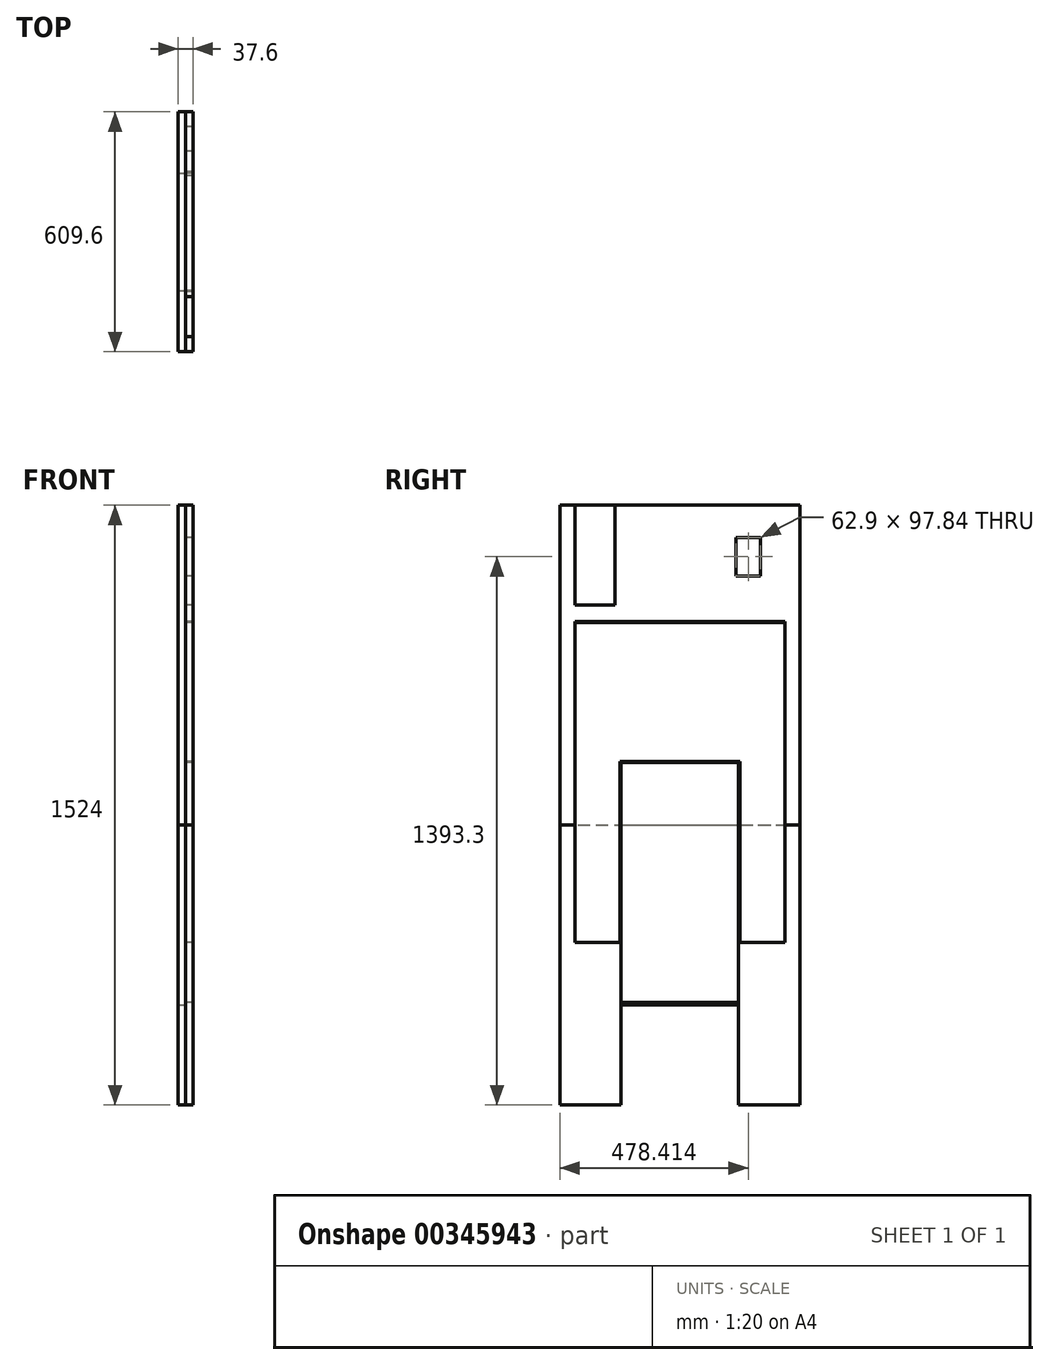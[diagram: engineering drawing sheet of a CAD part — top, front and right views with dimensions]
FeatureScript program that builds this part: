
annotation { "Feature Type Name" : "Feature", "Feature Type Description" : "" }
export const myFeature = defineFeature(function(context is Context, id is Id, definition is map)
    precondition{}
    {
        {
            var Q0;
            Q0=qCreatedBy(makeId("Right.planeOp"),FACE);
            var sketch = newSketch(context, id + "F0", { "sketchPlane" : qUnion([Q0])});
            skLineSegment(sketch, "E0.bottom", {"start": v(0, 0) * mm, "end": v(609.6, 0) * mm});
            skLineSegment(sketch, "E0.top", {"start": v(0, 1524) * mm, "end": v(609.6, 1524) * mm});
            skLineSegment(sketch, "E0.left", {"start": v(0, 0) * mm, "end": v(0, 1524) * mm});
            skLineSegment(sketch, "E0.right", {"start": v(609.6, 0) * mm, "end": v(609.6, 1524) * mm});
            skLineSegment(sketch, "E1", {"start": v(139.7, 1524) * mm, "end": v(139.7, 1270) * mm});
            skLineSegment(sketch, "E2", {"start": v(139.7, 1270) * mm, "end": v(0, 1270) * mm});
            skLineSegment(sketch, "E3.bottom", {"start": v(509.86, 1442.22) * mm, "end": v(446.97, 1442.22) * mm});
            skLineSegment(sketch, "E3.top", {"start": v(509.86, 1344.38) * mm, "end": v(446.97, 1344.38) * mm});
            skLineSegment(sketch, "E3.left", {"start": v(509.86, 1442.22) * mm, "end": v(509.86, 1344.38) * mm});
            skLineSegment(sketch, "E3.right", {"start": v(446.97, 1442.22) * mm, "end": v(446.97, 1344.38) * mm});
            skLineSegment(sketch, "E4", {"start": v(38.1, 1225.55) * mm, "end": v(38.1, 412.75) * mm});
            skLineSegment(sketch, "E5", {"start": v(38.1, 412.75) * mm, "end": v(152.4, 412.75) * mm});
            skLineSegment(sketch, "E6", {"start": v(152.4, 412.75) * mm, "end": v(152.4, 873.12) * mm});
            skLineSegment(sketch, "E7", {"start": v(152.4, 873.12) * mm, "end": v(457.2, 873.12) * mm});
            skLineSegment(sketch, "E8", {"start": v(457.2, 873.12) * mm, "end": v(457.2, 412.75) * mm});
            skLineSegment(sketch, "E9", {"start": v(457.2, 412.75) * mm, "end": v(571.5, 412.75) * mm});
            skLineSegment(sketch, "E10", {"start": v(571.5, 412.75) * mm, "end": v(571.5, 1225.55) * mm});
            skLineSegment(sketch, "E11", {"start": v(571.5, 1225.55) * mm, "end": v(463.88, 1225.55) * mm});
            skLineSegment(sketch, "E12", {"start": v(463.88, 1225.55) * mm, "end": v(463.88, 1169.64) * mm});
            skLineSegment(sketch, "E13", {"start": v(463.88, 1169.64) * mm, "end": v(403.31, 1169.64) * mm});
            skLineSegment(sketch, "E14", {"start": v(403.31, 1169.64) * mm, "end": v(403.31, 1225.55) * mm});
            skLineSegment(sketch, "E15", {"start": v(403.31, 1225.55) * mm, "end": v(206.29, 1225.55) * mm});
            skLineSegment(sketch, "E16", {"start": v(206.29, 1225.55) * mm, "end": v(206.29, 1169.64) * mm});
            skLineSegment(sketch, "E17", {"start": v(206.29, 1169.64) * mm, "end": v(145.72, 1169.64) * mm});
            skLineSegment(sketch, "E18", {"start": v(145.72, 1169.64) * mm, "end": v(145.72, 1225.55) * mm});
            skLineSegment(sketch, "E19", {"start": v(145.72, 1225.55) * mm, "end": v(38.1, 1225.55) * mm});
            skLineSegment(sketch, "E20.bottom", {"start": v(155.58, 869.95) * mm, "end": v(454.02, 869.95) * mm});
            skLineSegment(sketch, "E20.top", {"start": v(155.58, 260.35) * mm, "end": v(454.02, 260.35) * mm});
            skLineSegment(sketch, "E20.left", {"start": v(155.58, 869.95) * mm, "end": v(155.58, 260.35) * mm});
            skLineSegment(sketch, "E20.right", {"start": v(454.02, 869.95) * mm, "end": v(454.02, 260.35) * mm});
            skLineSegment(sketch, "E21.bottom", {"start": v(155.58, 0) * mm, "end": v(454.02, 0) * mm});
            skLineSegment(sketch, "E21.top", {"start": v(155.58, 254) * mm, "end": v(454.02, 254) * mm});
            skLineSegment(sketch, "E21.left", {"start": v(155.58, 0) * mm, "end": v(155.58, 254) * mm});
            skLineSegment(sketch, "E21.right", {"start": v(454.02, 0) * mm, "end": v(454.02, 254) * mm});
            skLineSegment(sketch, "E22", {"start": v(38.1, 1225.55) * mm, "end": v(0, 1225.55) * mm, "construction": true});
            skLineSegment(sketch, "E23", {"start": v(609.6, 1225.55) * mm, "end": v(571.5, 1225.55) * mm, "construction": true});
            skLineSegment(sketch, "E24", {"start": v(155.58, 873.12) * mm, "end": v(155.58, 869.95) * mm, "construction": true});
            skLineSegment(sketch, "E25", {"start": v(155.58, 869.95) * mm, "end": v(152.4, 869.95) * mm, "construction": true});
            skLineSegment(sketch, "E26", {"start": v(454.02, 869.95) * mm, "end": v(457.2, 869.95) * mm, "construction": true});
            skLineSegment(sketch, "E27", {"start": v(145.72, 1225.55) * mm, "end": v(463.88, 1225.55) * mm});
            skLineSegment(sketch, "E28", {"start": v(38.1, 1524) * mm, "end": v(38.1, 1270) * mm});
            skLineSegment(sketch, "E29", {"start": v(0, 711.2) * mm, "end": v(38.1, 711.2) * mm});
            skLineSegment(sketch, "E30", {"start": v(571.5, 711.2) * mm, "end": v(609.6, 711.2) * mm});
            skLineSegment(sketch, "E31", {"start": v(38.1, 711.2) * mm, "end": v(571.5, 711.2) * mm});
            skLineSegment(sketch, "E32", {"start": v(571.5, 1225.55) * mm, "end": v(571.5, 1228.73) * mm});
            skLineSegment(sketch, "E33", {"start": v(571.5, 1228.73) * mm, "end": v(38.1, 1228.73) * mm});
            skLineSegment(sketch, "E34", {"start": v(38.1, 1228.73) * mm, "end": v(38.1, 1225.55) * mm});
            skLineSegment(sketch, "E35", {"start": v(155.57, 260.35) * mm, "end": v(155.57, 254) * mm});
            skLineSegment(sketch, "E36", {"start": v(454.02, 260.35) * mm, "end": v(454.02, 254) * mm});
            skLineSegment(sketch, "E37", {"start": v(152.4, 412.75) * mm, "end": v(155.58, 412.75) * mm});
            skLineSegment(sketch, "E38", {"start": v(454.02, 412.75) * mm, "end": v(457.2, 412.75) * mm});
            skSolve(sketch);
        }
        {
            var Q0;
            {var subQ12=sQuery(id+"F0.wireOp",EDGE,"E5");Q0=makeQuery(id+"F0.imprint","IMPRINT",FACE,{"disambiguationData":[TD([[makeQuery(id+"F0.imprint","IMPRINT",EDGE,{"derivedFrom":subQ12}),-1.0]])]});}
            var Q1;
            Q1=makeQuery(id+"F0.imprint","IMPRINT",FACE,{"disambiguationData":[TD([[makeQuery(id+"F0.imprint","IMPRINT",EDGE,{"derivedFrom":sQuery(id+"F0.wireOp",EDGE,"E21.bottom")}),1.0]])]});
            var Q2;
            {var subQ0=sQuery(id+"F0.wireOp",EDGE,"E20.top");Q2=makeQuery(id+"F0.imprint","IMPRINT",FACE,{"disambiguationData":[TD([[makeQuery(id+"F0.imprint","IMPRINT",EDGE,{"derivedFrom":subQ0}),1.0]])]});}
            var Q3;
            {var subQ0=sQuery(id+"F0.wireOp",EDGE,"E5");Q3=makeQuery(id+"F0.imprint","IMPRINT",FACE,{"disambiguationData":[TD([[makeQuery(id+"F0.imprint","IMPRINT",EDGE,{"derivedFrom":subQ0}),1.0]])]});}
            var Q4;
            Q4=makeQuery(id+"F0.imprint","IMPRINT",FACE,{"disambiguationData":[TD([[makeQuery(id+"F0.imprint","IMPRINT",EDGE,{"derivedFrom":sQuery(id+"F0.wireOp",EDGE,"E20.top")}),-1.0]])]});
            var Q5;
            {var subQ0=sQuery(id+"F0.wireOp",EDGE,"E9");Q5=makeQuery(id+"F0.imprint","IMPRINT",FACE,{"disambiguationData":[TD([[makeQuery(id+"F0.imprint","IMPRINT",EDGE,{"derivedFrom":subQ0}),-1.0]])]});}
            var Q6;
            {var subQ0=sQuery(id+"F0.wireOp",EDGE,"E9");Q6=makeQuery(id+"F0.imprint","IMPRINT",FACE,{"disambiguationData":[TD([[makeQuery(id+"F0.imprint","IMPRINT",EDGE,{"derivedFrom":subQ0}),1.0]])]});}
            var Q7;
            {var subQ0=sQuery(id+"F0.wireOp",EDGE,"E38");Q7=makeQuery(id+"F0.imprint","IMPRINT",FACE,{"disambiguationData":[TD([[makeQuery(id+"F0.imprint","IMPRINT",EDGE,{"derivedFrom":subQ0}),1.0]])]});}
            var Q8;
            {var subQ0=sQuery(id+"F0.wireOp",EDGE,"E37");Q8=makeQuery(id+"F0.imprint","IMPRINT",FACE,{"disambiguationData":[TD([[makeQuery(id+"F0.imprint","IMPRINT",EDGE,{"derivedFrom":subQ0}),1.0]])]});}
            extrude(context, id + "F1", {"entities" : qUnion([Q0, Q1, Q2, Q3, Q4, Q5, Q6, Q7, Q8]), "oppositeDirection" : true, "depth" : 18.8 * mm});
        }
        {
            var Q0;
            Q0=makeQuery(id+"F0.imprint","IMPRINT",FACE,{"disambiguationData":[TD([[makeQuery(id+"F0.imprint","IMPRINT",EDGE,{"derivedFrom":sQuery(id+"F0.wireOp",EDGE,"E21.bottom")}),1.0]])]});
            var Q1;
            {var subQ0=sQuery(id+"F0.wireOp",EDGE,"E20.top");Q1=makeQuery(id+"F0.imprint","IMPRINT",FACE,{"disambiguationData":[TD([[makeQuery(id+"F0.imprint","IMPRINT",EDGE,{"derivedFrom":subQ0}),1.0]])]});}
            var Q2;
            {var subQ10=sQuery(id+"F0.wireOp",EDGE,"E7");Q2=makeQuery(id+"F0.imprint","IMPRINT",FACE,{"disambiguationData":[TD([[makeQuery(id+"F0.imprint","IMPRINT",EDGE,{"derivedFrom":subQ10}),1.0]])]});}
            var Q3;
            {var subQ0=sQuery(id+"F0.wireOp",EDGE,"E9");Q3=makeQuery(id+"F0.imprint","IMPRINT",FACE,{"disambiguationData":[TD([[makeQuery(id+"F0.imprint","IMPRINT",EDGE,{"derivedFrom":subQ0}),1.0]])]});}
            var Q4;
            {var subQ0=sQuery(id+"F0.wireOp",EDGE,"E5");Q4=makeQuery(id+"F0.imprint","IMPRINT",FACE,{"disambiguationData":[TD([[makeQuery(id+"F0.imprint","IMPRINT",EDGE,{"derivedFrom":subQ0}),1.0]])]});}
            var Q5;
            {var subQ0=sQuery(id+"F0.wireOp",EDGE,"E16");Q5=makeQuery(id+"F0.imprint","IMPRINT",FACE,{"disambiguationData":[TD([[makeQuery(id+"F0.imprint","IMPRINT",EDGE,{"derivedFrom":subQ0}),-1.0]])]});}
            var Q6;
            {var subQ0=sQuery(id+"F0.wireOp",EDGE,"E12");Q6=makeQuery(id+"F0.imprint","IMPRINT",FACE,{"disambiguationData":[TD([[makeQuery(id+"F0.imprint","IMPRINT",EDGE,{"derivedFrom":subQ0}),-1.0]])]});}
            var Q7;
            {var subQ0=sQuery(id+"F0.wireOp",EDGE,"E20.bottom");Q7=makeQuery(id+"F0.imprint","IMPRINT",FACE,{"disambiguationData":[TD([[makeQuery(id+"F0.imprint","IMPRINT",EDGE,{"derivedFrom":subQ0}),-1.0]])]});}
            extrude(context, id + "F2", {"entities" : qUnion([Q0, Q1, Q2, Q3, Q4, Q5, Q6, Q7]), "depth" : 18.8 * mm});
        }
        {
            var Q0;
            {var subQ0=sQuery(id+"F0.wireOp",EDGE,"E9");Q0=makeQuery(id+"F0.imprint","IMPRINT",FACE,{"disambiguationData":[TD([[makeQuery(id+"F0.imprint","IMPRINT",EDGE,{"derivedFrom":subQ0}),-1.0]])]});}
            var Q1;
            {var subQ0=sQuery(id+"F0.wireOp",EDGE,"E5");Q1=makeQuery(id+"F0.imprint","IMPRINT",FACE,{"disambiguationData":[TD([[makeQuery(id+"F0.imprint","IMPRINT",EDGE,{"derivedFrom":subQ0}),-1.0]])]});}
            extrude(context, id + "F3", {"entities" : qUnion([Q0, Q1]), "depth" : 18.8 * mm});
        }
        {
            var Q0;
            {var subQ5=sQuery(id+"F0.wireOp",EDGE,"E1");Q0=makeQuery(id+"F0.imprint","IMPRINT",FACE,{"disambiguationData":[TD([[makeQuery(id+"F0.imprint","IMPRINT",EDGE,{"derivedFrom":subQ5}),1.0]])]});}
            var Q1;
            {var subQ3=sQuery(id+"F0.wireOp",EDGE,"E28");Q1=makeQuery(id+"F0.imprint","IMPRINT",FACE,{"disambiguationData":[TD([[makeQuery(id+"F0.imprint","IMPRINT",EDGE,{"derivedFrom":subQ3}),-1.0]])]});}
            extrude(context, id + "F4", {"entities" : qUnion([Q0, Q1]), "depth" : 18.8 * mm});
        }
        {
            var Q0;
            {var subQ0=sQuery(id+"F0.wireOp",EDGE,"E1");Q0=makeQuery(id+"F0.imprint","IMPRINT",FACE,{"disambiguationData":[TD([[makeQuery(id+"F0.imprint","IMPRINT",EDGE,{"derivedFrom":subQ0}),-1.0]])]});}
            var Q1;
            Q1=makeQuery(id+"F0.imprint","IMPRINT",FACE,{"disambiguationData":[TD([[makeQuery(id+"F0.imprint","IMPRINT",EDGE,{"derivedFrom":sQuery(id+"F0.wireOp",EDGE,"E3.bottom")}),1.0]])]});
            var Q2;
            {var subQ0=sQuery(id+"F0.wireOp",EDGE,"E12");Q2=makeQuery(id+"F0.imprint","IMPRINT",FACE,{"disambiguationData":[TD([[makeQuery(id+"F0.imprint","IMPRINT",EDGE,{"derivedFrom":subQ0}),-1.0]])]});}
            var Q3;
            {var subQ0=sQuery(id+"F0.wireOp",EDGE,"E16");Q3=makeQuery(id+"F0.imprint","IMPRINT",FACE,{"disambiguationData":[TD([[makeQuery(id+"F0.imprint","IMPRINT",EDGE,{"derivedFrom":subQ0}),-1.0]])]});}
            var Q4;
            {var subQ0=sQuery(id+"F0.wireOp",EDGE,"E20.bottom");Q4=makeQuery(id+"F0.imprint","IMPRINT",FACE,{"disambiguationData":[TD([[makeQuery(id+"F0.imprint","IMPRINT",EDGE,{"derivedFrom":subQ0}),-1.0]])]});}
            var Q5;
            {var subQ1=sQuery(id+"F0.wireOp",EDGE,"E7");Q5=makeQuery(id+"F0.imprint","IMPRINT",FACE,{"disambiguationData":[TD([[makeQuery(id+"F0.imprint","IMPRINT",EDGE,{"derivedFrom":subQ1}),-1.0]])]});}
            var Q6;
            {var subQ4=sQuery(id+"F0.wireOp",EDGE,"E11");Q6=makeQuery(id+"F0.imprint","IMPRINT",FACE,{"disambiguationData":[TD([[makeQuery(id+"F0.imprint","IMPRINT",EDGE,{"derivedFrom":subQ4}),-1.0]])]});}
            var Q7;
            {var subQ5=sQuery(id+"F0.wireOp",EDGE,"E1");Q7=makeQuery(id+"F0.imprint","IMPRINT",FACE,{"disambiguationData":[TD([[makeQuery(id+"F0.imprint","IMPRINT",EDGE,{"derivedFrom":subQ5}),1.0]])]});}
            var Q8;
            {var subQ10=sQuery(id+"F0.wireOp",EDGE,"E7");Q8=makeQuery(id+"F0.imprint","IMPRINT",FACE,{"disambiguationData":[TD([[makeQuery(id+"F0.imprint","IMPRINT",EDGE,{"derivedFrom":subQ10}),1.0]])]});}
            var Q9;
            {var subQ3=sQuery(id+"F0.wireOp",EDGE,"E28");Q9=makeQuery(id+"F0.imprint","IMPRINT",FACE,{"disambiguationData":[TD([[makeQuery(id+"F0.imprint","IMPRINT",EDGE,{"derivedFrom":subQ3}),-1.0]])]});}
            extrude(context, id + "F5", {"entities" : qUnion([Q0, Q1, Q2, Q3, Q4, Q5, Q6, Q7, Q8, Q9]), "oppositeDirection" : true, "depth" : 18.8 * mm});
        }
    });
